# Revit family: FallProtection_RopeAccessNeedle_Kattsafe_400AFrame
name_source: partatom
category: Specialty Equipment
units: mm (PartAtom-declared; Revit-internal decimal feet)

## family parameters
Always vertical = Yes
Cut with Voids When Loaded = No
Enable Cutting in Views = No
Maintain Annotation Orientation = No
OmniClass Number = 23.27.71.21
Part Type = Normal
Room Calculation Point = No
Round Connector Dimension = Use Diameter
Shared = No
Work Plane-Based = No

## types (10) — shared parameters
Assembly Code = E1090100
Description = Kattsafe needles are designed for rope access on roofs where the load needs to be spread to avoid damaging the roof area, and for roofs with no parapets.
ElementType = Fall Protection
Export Type to IFC As = IfcBuildingElementProxyType
FramePinHeight = 406 mm  [stored 1.33202 ft]
IfcExportAs = IfcBuildingElementProxyType
IfcExportType = USERDEFINED
Manufacturer = Kattsafe®
ManufacturerOverallWidth = 760 mm  [stored 2.49344 ft]
ManufacturerURLProductSpecific = https://kattsafe.com.au
Material = Aluminum_Kattsafe_Satin
ModifiedIssue = 20240430 $
RearAttachmentType = Rearattachment_Kattsafe_Needle : Horizontal Trolley (OH448A)
Type IFC Predefined Type = USERDEFINED
URL = https://kattsafe.com.au
Uniclass2015Code = Pr_40_70_75_21
Uniclass2015Title = Davit arms
Uniclass2015Version = Products v1.23
zero-valued in all types: Default Elevation

## per-type parameters (varying)
| type | 1200Extension | 1500Extension | ExtendableBoom | MainBoomCenterExtension | ManufacturerSpecCode | Model | RearBeamAngledHeightCalc | RearBeamHeight | RearBeamWidth | RearFixingHeight | RearMemberFixingPointCalc | TrolleyAlignOffset | Type Comments |
| 1500 Cantilever - Horizontal Trolley (OH404.1500 + OH448A) | No | Yes | Yes | 975 mm  [stored 3.19882 ft] | OH404.15 + OH448A | OH404.15 + OH448A | 170 mm  [stored 0.557743 ft] | 190 mm | 70 mm  [stored 0.229659 ft] | 42 mm  [stored 0.137795 ft] | 75 mm | 15 mm  [stored 0.0492126 ft] | 400mm A-Frame - 1500mm Extension - Horizontal Trolley Rear Attachment |
| 1500 Cantilever - Vertical Trolley (OH404.1500 + OH449A) | No | Yes | Yes | 975 mm  [stored 3.19882 ft] | OH404.15 + OH449A | OH404.15 + OH449A | 170 mm  [stored 0.557743 ft] | 190 mm | 70 mm  [stored 0.229659 ft] | 67 mm | 75 mm | 33 mm  [stored 0.108268 ft] | 400mm A-Frame - 1500mm Extension - Vertical Trolley Rear Attachment |
| 1500 Cantilever - Wide Deck Mount (OH404.1500 + OH444W) | No | Yes | Yes | 975 mm  [stored 3.19882 ft] | OH404.15 + OH444W | OH404.15 + OH444W | 170 mm  [stored 0.557743 ft] | 190 mm | 70 mm  [stored 0.229659 ft] | 125 mm  [stored 0.410105 ft] | 75 mm | 0 mm  [stored 0 ft] | 400mm A-Frame - 1500mm Extension - Wide Deck Mount Rear Attachment |
| 1500 Cantilever - Metal Deck Mount (OH404.1500 + OH444A) | No | Yes | Yes | 975 mm  [stored 3.19882 ft] | OH404.15 + OH444A | OH404.15 + OH444A | 170 mm  [stored 0.557743 ft] | 190 mm | 70 mm  [stored 0.229659 ft] | 123 mm  [stored 0.403543 ft] | 75 mm | 0 mm  [stored 0 ft] | 400mm A-Frame - 1500mm Extension - Metal Deck Mount Rear Attachment |
| 1500 Cantilever - Concrete Mount (OH404.1500 + OH443) | No | Yes | Yes | 975 mm  [stored 3.19882 ft] | OH404.15 + OH443 | OH404.15 + OH443 | 170 mm  [stored 0.557743 ft] | 190 mm | 70 mm  [stored 0.229659 ft] | 119 mm  [stored 0.39042 ft] | 75 mm | 0 mm  [stored 0 ft] | 400mm A-Frame - 1500mm Extension - Concrete Mount Rear Attachment |
| 1200 Cantilever - Horizontal Trolley (OH404.1200 + OH448A) | Yes | No | No | 0 mm  [stored 0 ft] | OH404.12 + OH448A | OH404.12 + OH448A | 160 mm  [stored 0.524934 ft] | 180 mm  [stored 0.590551 ft] | 60 mm  [stored 0.19685 ft] | 42 mm  [stored 0.137795 ft] | 70 mm  [stored 0.229659 ft] | 15 mm  [stored 0.0492126 ft] | 400mm A-Frame - 1200mm Extension - Horizontal Trolley Rear Attachment |
| 1200 Cantilever - Vertical Trolley (OH404.1200 + OH449A) | Yes | No | No | 0 mm  [stored 0 ft] | OH404.12 + OH449A | OH404.12 + OH449A | 160 mm  [stored 0.524934 ft] | 180 mm  [stored 0.590551 ft] | 60 mm  [stored 0.19685 ft] | 67 mm | 70 mm  [stored 0.229659 ft] | 33 mm  [stored 0.108268 ft] | 400mm A-Frame - 1200mm Extension - Vertical Trolley Rear Attachment |
| 1200 Cantilever - Wide Deck Mount (OH404.1200 + OH444W) | Yes | No | No | 0 mm  [stored 0 ft] | OH404.12 + OH444W | OH404.12 + OH444W | 160 mm  [stored 0.524934 ft] | 180 mm  [stored 0.590551 ft] | 60 mm  [stored 0.19685 ft] | 125 mm  [stored 0.410105 ft] | 70 mm  [stored 0.229659 ft] | 0 mm  [stored 0 ft] | 400mm A-Frame - 1200mm Extension - Wide Deck Mount Rear Attachment |
| 1200 Cantilever - Metal Deck Mount (OH404.1200 + OH444A) | Yes | No | No | 0 mm  [stored 0 ft] | OH404.12 + OH444A | OH404.12 + OH444A | 160 mm  [stored 0.524934 ft] | 180 mm  [stored 0.590551 ft] | 60 mm  [stored 0.19685 ft] | 123 mm  [stored 0.403543 ft] | 70 mm  [stored 0.229659 ft] | 0 mm  [stored 0 ft] | 400mm A-Frame - 1200mm Extension - Metal Deck Mount Rear Attachment |
| 1200 Cantilever - Concrete Mount (OH404.1200 + OH443) | Yes | No | No | 0 mm  [stored 0 ft] | OH404.12 + OH443 | OH404.12 + OH443 | 160 mm  [stored 0.524934 ft] | 180 mm  [stored 0.590551 ft] | 60 mm  [stored 0.19685 ft] | 119 mm  [stored 0.39042 ft] | 70 mm  [stored 0.229659 ft] | 0 mm  [stored 0 ft] | 400mm A-Frame - 1200mm Extension - Concrete Mount Rear Attachment |

note: [stored X ft] marks values corroborated as IEEE doubles in the binary element streams (Revit-internal decimal feet)

## geometry (parser evidence)
native form markers: Sweep x6
no freeform markers — native parametric forms only
